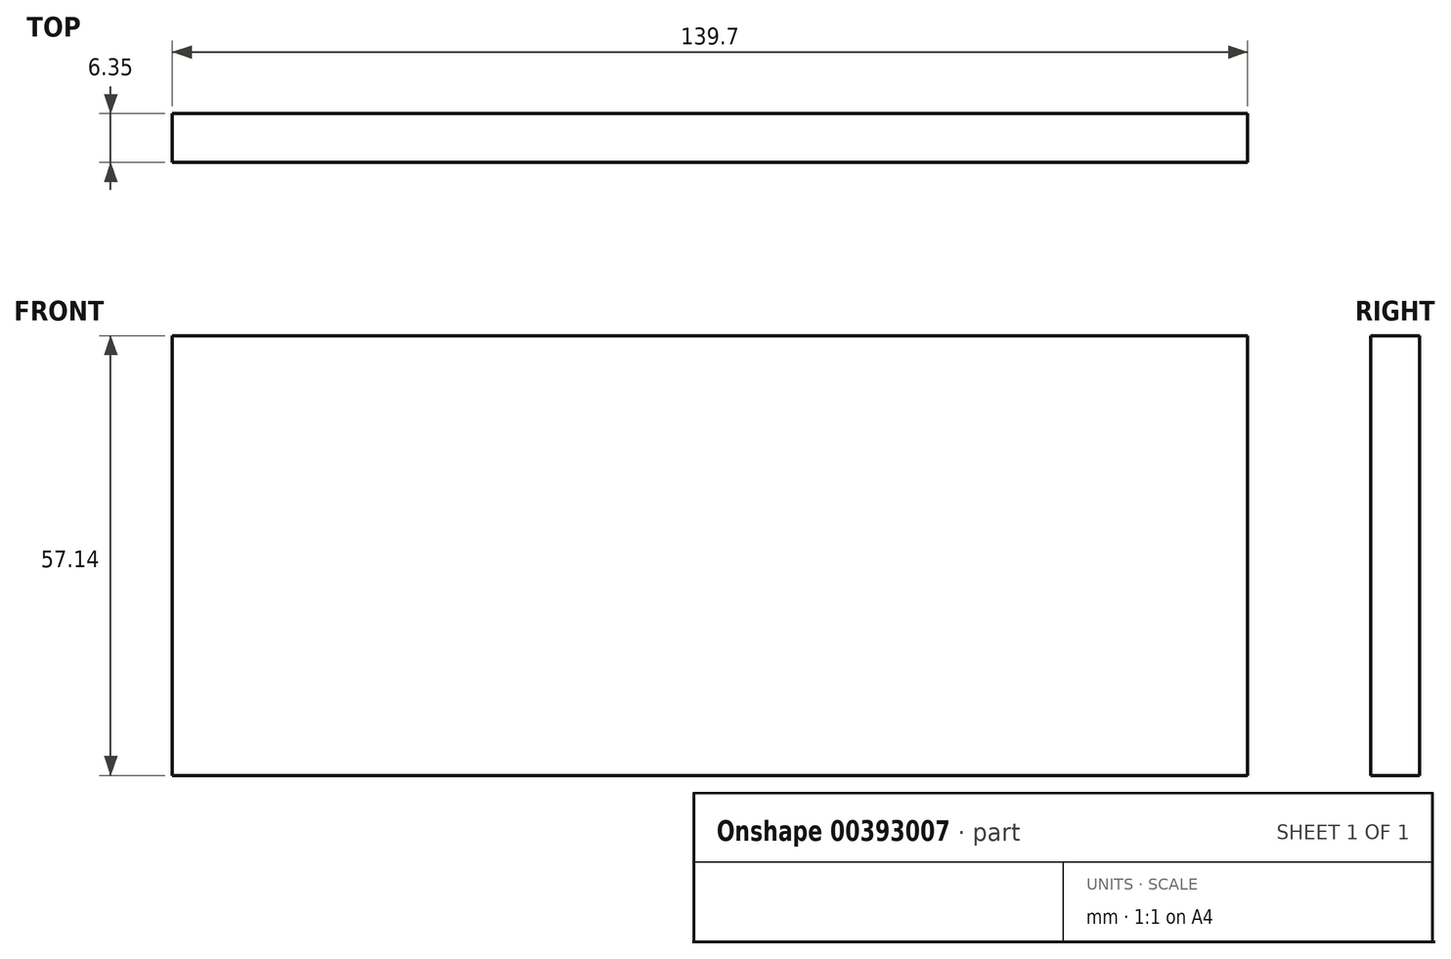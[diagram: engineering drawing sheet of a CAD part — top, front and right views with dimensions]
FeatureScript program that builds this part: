
annotation { "Feature Type Name" : "Feature", "Feature Type Description" : "" }
export const myFeature = defineFeature(function(context is Context, id is Id, definition is map)
    precondition{}
    {
        {
            var Q0;
            Q0=qCreatedBy(makeId("Front.planeOp"),FACE);
            var sketch = newSketch(context, id + "F0", { "sketchPlane" : qUnion([Q0])});
            skLineSegment(sketch, "E0.bottom", {"start": v(69.85, -28.58) * mm, "end": v(-69.85, -28.58) * mm});
            skLineSegment(sketch, "E0.top", {"start": v(69.85, 28.58) * mm, "end": v(-69.85, 28.58) * mm});
            skLineSegment(sketch, "E0.left", {"start": v(69.85, -28.58) * mm, "end": v(69.85, 28.57) * mm});
            skLineSegment(sketch, "E0.right", {"start": v(-69.85, -28.58) * mm, "end": v(-69.85, 28.57) * mm});
            skPoint(sketch, "E0.middle", {"position": v(0, 0) * mm});
            skSolve(sketch);
        }
        {
            var Q0;
            Q0 = qSketchRegion(id + "F0", true);
            extrude(context, id + "F1", {"entities" : qUnion([Q0]), "depth" : 6.35 * mm});
        }
    });
